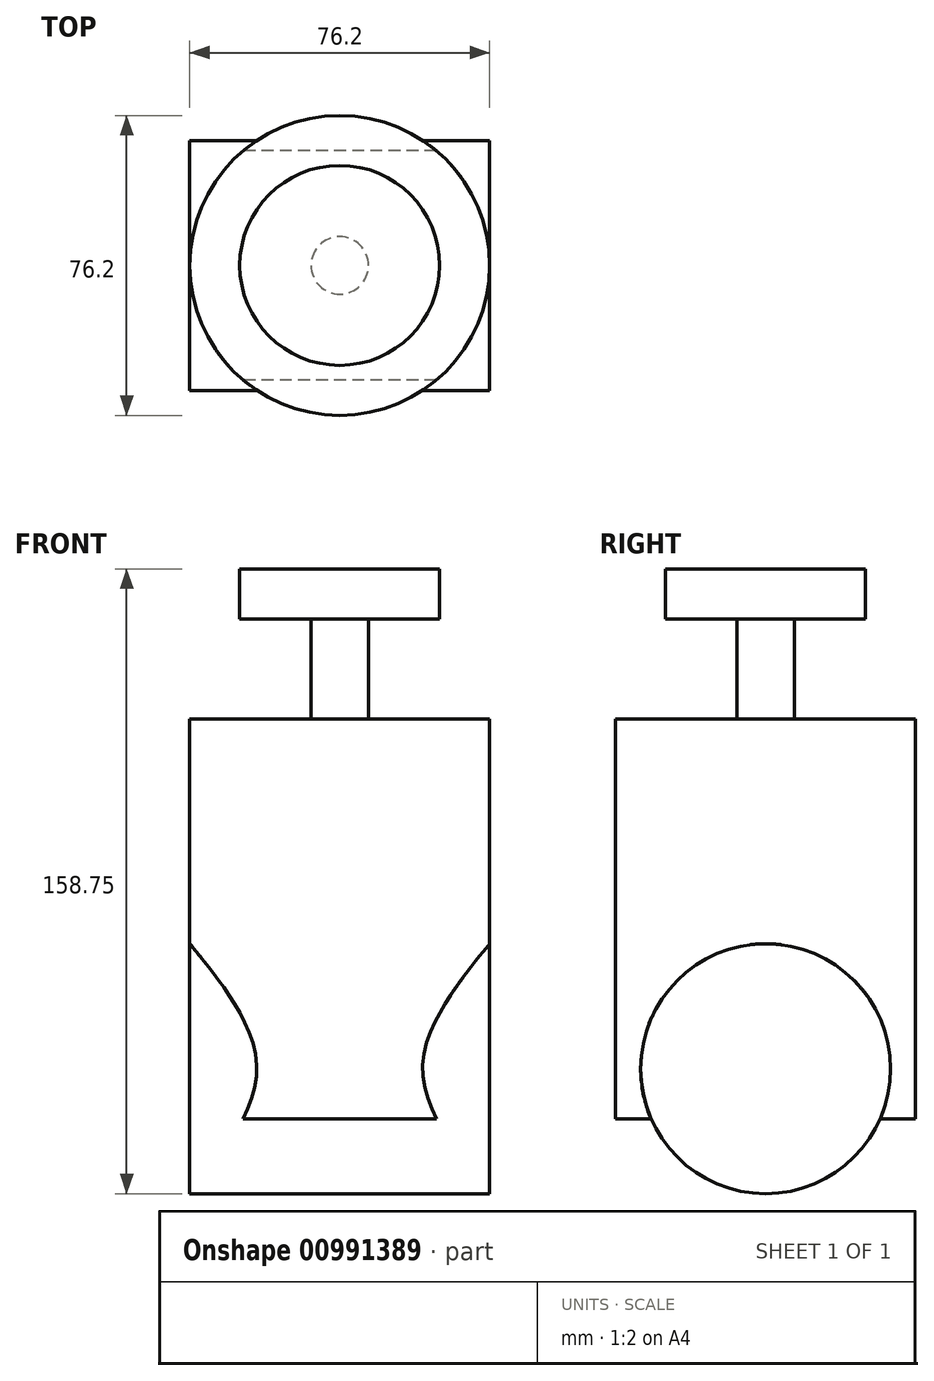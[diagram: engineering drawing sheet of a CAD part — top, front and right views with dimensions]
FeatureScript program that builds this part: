
annotation { "Feature Type Name" : "Feature", "Feature Type Description" : "" }
export const myFeature = defineFeature(function(context is Context, id is Id, definition is map)
    precondition{}
    {
        {
            var Q0;
            Q0=qCreatedBy(makeId("Top.planeOp"),FACE);
            var sketch = newSketch(context, id + "F0", { "sketchPlane" : qUnion([Q0])});
            skCircle(sketch, "E0", {"center": v(0, 0) * mm, "radius": 38.1 * mm});
            skSolve(sketch);
        }
        {
            var Q0;
            Q0=qSketchRegion(id+"F0",true);
            extrude(context, id + "F1", {"entities" : qUnion([Q0]), "endBound" : BoundingType.SYMMETRIC, "depth" : 101.6 * mm, "offsetDistance" : 25.4 * mm});
        }
        {
            var Q0;
            Q0=qCreatedBy(makeId("Right.planeOp"),FACE);
            var sketch = newSketch(context, id + "F2", { "sketchPlane" : qUnion([Q0])});
            skCircle(sketch, "E1", {"center": v(0, -38.1) * mm, "radius": 31.75 * mm});
            skSolve(sketch);
        }
        {
            var Q0;
            Q0=qSketchRegion(id+"F2",true);
            extrude(context, id + "F3", {"entities" : qUnion([Q0]), "operationType" : NewBodyOperationType.ADD, "endBound" : BoundingType.SYMMETRIC, "depth" : 76.2 * mm, "offsetDistance" : 25.4 * mm});
        }
        {
            var Q0;
            Q0=makeQuery(id+"F1.opExtrude","CAP_FACE",FACE,{"disambiguationData":[OSD([sQuery(id+"F0.wireOp",EDGE,"E0")])],"isStart":false});
            var sketch = newSketch(context, id + "F4", { "sketchPlane" : qUnion([Q0])});
            skCircle(sketch, "E2", {"center": v(0, 0) * mm, "radius": 7.3 * mm});
            skSolve(sketch);
        }
        {
            var Q0;
            Q0=qSketchRegion(id+"F4",true);
            extrude(context, id + "F5", {"entities" : qUnion([Q0]), "depth" : 25.4 * mm, "offsetDistance" : 25.4 * mm});
        }
        {
            var Q0;
            Q0=makeQuery(id+"F5.opExtrude","CAP_FACE",FACE,{"disambiguationData":[OSD([sQuery(id+"F4.wireOp",EDGE,"E2")])],"isStart":false});
            var sketch = newSketch(context, id + "F6", { "sketchPlane" : qUnion([Q0])});
            skCircle(sketch, "E3", {"center": v(0, 0) * mm, "radius": 25.4 * mm});
            skSolve(sketch);
        }
        {
            var Q0;
            Q0=qSketchRegion(id+"F6",true);
            extrude(context, id + "F7", {"entities" : qUnion([Q0]), "depth" : 12.7 * mm, "offsetDistance" : 25.4 * mm});
        }
    });
